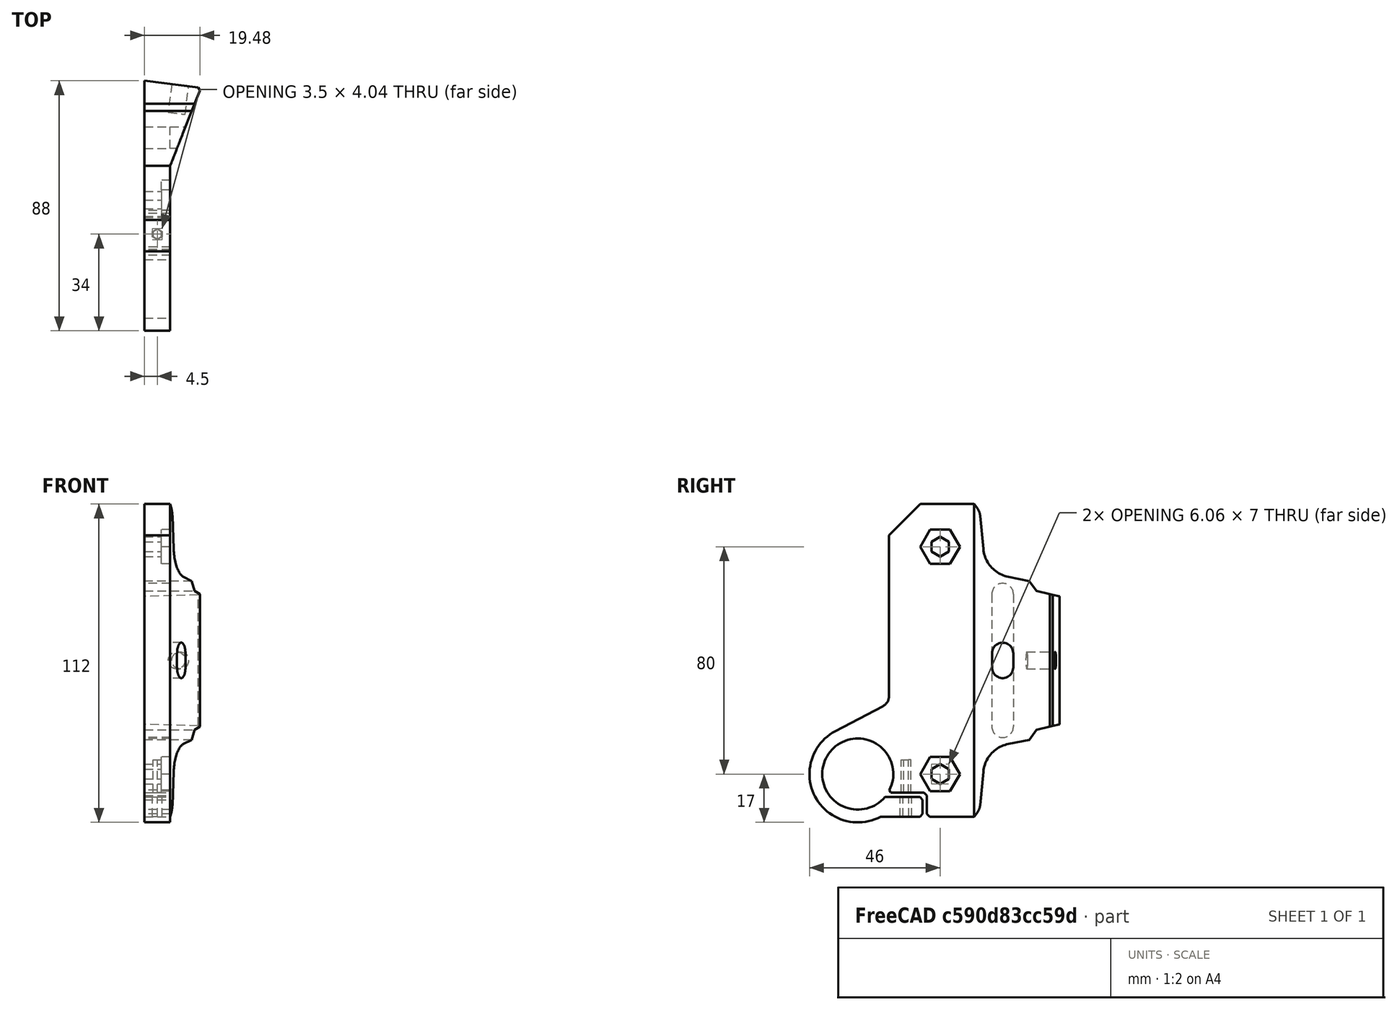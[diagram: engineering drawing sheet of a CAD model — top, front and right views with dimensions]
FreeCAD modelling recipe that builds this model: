
FCSTD DOCUMENT  (FreeCAD 0.19R)
Label: TailLightBracketForRack_80mmDual
License: All rights reserved
LicenseURL: http://en.wikipedia.org/wiki/All_rights_reserved
objects: Sketcher::SketchObject×12, PartDesign::Pocket×11, PartDesign::Fillet×3, PartDesign::Chamfer×3, PartDesign::Pad×1, PartDesign::Body×1, App::Part×1, Mesh::Feature×1
note: 49 computed .brp shape members not serialized (recipe doc carries the construction recipe); baked Part::Feature solids carry a one-line shape summary decoded from their .brp

FEATURE [Sketcher::SketchObject] Sketch007  label="body"
  FullyConstrained = true
  MapMode = 5
  Support = -> [XY_Plane001]
  sketch-geometry (5):
    g0: LineSegment StartX=9 StartY=0 StartZ=0 EndX=19.8509 EndY=27.5626 EndZ=0
    g1: LineSegment StartX=19.8509 StartY=27.5626 StartZ=0 EndX=0 EndY=30 EndZ=0
    g2: LineSegment StartX=9 StartY=0 StartZ=0 EndX=9 EndY=-60 EndZ=0
    g3: LineSegment StartX=9 StartY=-60 StartZ=0 EndX=0 EndY=-60 EndZ=0
    g4: LineSegment StartX=0 StartY=-60 StartZ=0 EndX=0 EndY=30 EndZ=0
  constraints (15):
    c: PointOnObject(g0,g-1)
    c: Angle(g1) = 3.01942
    c: Coincident(g0,g1)
    c: DistanceY(g1) = 30
    c: Distance(g1) = 20
    c: Coincident(g2,g0)
    c: Vertical(g2)
    c: Coincident(g3,g2)
    c: PointOnObject(g3,g-2)
    c: Horizontal(g3)
    c: Coincident(g4,g3)
    c: Vertical(g4)
    c: Coincident(g4,g1)
    c: Distance(g3) = 9
    c: DistanceY(g3) = -60
FEATURE [PartDesign::Pad] Pad
  AllowMultiFace = false
  Direction = (1,1,1)
  Length = 200
  Length2 = 100
  Midplane = true
  Profile = -> Sketch007
  Type = 0
FEATURE [Sketcher::SketchObject] Sketch012  label="bodypocket1"
  FullyConstrained = false
  MapMode = 5
  Placement = pos=(-30,0,0) rot=(0.57735,-0.57735,-0.57735;2.0944rad)
  sketch-geometry (23):
    g0: LineSegment StartX=-105.867 StartY=145.328 StartZ=0 EndX=-105.867 EndY=-150.387 EndZ=0
    g1: LineSegment StartX=-30.0416 StartY=-22.5 StartZ=0 EndX=-30.0416 EndY=22.5 EndZ=0
    g2: LineSegment StartX=195.435 StartY=55 StartZ=0 EndX=195.435 EndY=105.454 EndZ=0
    g3: LineSegment StartX=195.435 StartY=105.454 StartZ=0 EndX=-105.867 EndY=145.328 EndZ=0
    g4: LineSegment StartX=195.435 StartY=55 StartZ=0 EndX=0 EndY=55 EndZ=0
    g5: LineSegment StartX=0 StartY=55 StartZ=0 EndX=-21.9085 EndY=24.4142 EndZ=0
    g6: LineSegment StartX=33 StartY=-55 StartZ=0 EndX=0 EndY=-55 EndZ=0
    g7: LineSegment StartX=0 StartY=-55 StartZ=0 EndX=-21.9085 EndY=-24.4142 EndZ=0
    g8: ArcOfCircle CenterX=41 CenterY=-40 CenterZ=0 NormalX=0 NormalY=0 NormalZ=1 AngleXU=0 Radius=17 StartAngle=4.22243 EndAngle=7.36952
    g9: LineSegment StartX=48.9175 StartY=-24.9563 StartZ=0 EndX=30 EndY=-15 EndZ=0
    g10: Circle CenterX=41 CenterY=-40 CenterZ=0 NormalX=0 NormalY=0 NormalZ=1 AngleXU=0 Radius=12.5
    g11: LineSegment StartX=150.469 StartY=0 StartZ=0 EndX=97.2937 EndY=-143.387 EndZ=0
    g12: LineSegment StartX=97.2937 StartY=-143.387 StartZ=0 EndX=-105.867 EndY=-150.387 EndZ=0
    g13: LineSegment StartX=30 StartY=0 StartZ=0 EndX=150.469 EndY=0 EndZ=0
    g14: LineSegment StartX=-21.9085 StartY=24.4142 StartZ=0 EndX=-30.0416 EndY=22.5 EndZ=0
    g15: LineSegment StartX=-21.9085 StartY=-24.4142 StartZ=0 EndX=-30.0416 EndY=-22.5 EndZ=0
    g16: ArcOfCircle CenterX=-9 CenterY=23.25 CenterZ=0 NormalX=0 NormalY=0 NormalZ=1 AngleXU=0 Radius=3.75 StartAngle=0 EndAngle=3.14159
    g17: ArcOfCircle CenterX=-9 CenterY=-23.25 CenterZ=0 NormalX=0 NormalY=0 NormalZ=1 AngleXU=0 Radius=3.75 StartAngle=3.14159 EndAngle=6.28319
    g18: LineSegment StartX=-12.75 StartY=23.25 StartZ=0 EndX=-12.75 EndY=-23.25 EndZ=0
    g19: LineSegment StartX=-5.25 StartY=23.25 StartZ=0 EndX=-5.25 EndY=-23.25 EndZ=0
    g20: LineSegment StartX=-14.9249 StartY=27 StartZ=0 EndX=-4.09953 EndY=27 EndZ=0
    g21: LineSegment StartX=-14.2475 StartY=-27 StartZ=0 EndX=-3.85948 EndY=-27 EndZ=0
    g22: LineSegment StartX=30 StartY=-15 StartZ=0 EndX=30 EndY=0 EndZ=0
  constraints (50):
    c: Symmetric(g1,g1,g-1)
    c: Distance(g1) = 45
    c: Vertical(g0)
    c: Vertical(g2)
    c: Coincident(g3,g2)
    c: Coincident(g3,g0)
    c: PointOnObject(g4,g-2)
    c: Coincident(g4,g5)
    c: PointOnObject(g6,g-2)
    c: Coincident(g7,g6)
    c: DistanceX(g9) = 30
    c: Tangent(g9,g8) = -1.5708
    c: Diameter(g8) = 34
    c: Coincident(g10,g8)
    c: Diameter(g10) = 25
    c: DistanceY(g9) = -15
    c: Coincident(g11,g12)
    c: Coincident(g12,g0)
    c: PointOnObject(g13,g-1)
    c: Coincident(g11,g13)
    c: Symmetric(g5,g7,g-1)
    c: Coincident(g14,g5)
    c: Coincident(g14,g1)
    c: Coincident(g15,g7)
    c: Coincident(g15,g1)
    c: Tangent(g16,g19) = 1.5708
    c: Tangent(g16,g18) = -1.5708
    c: Tangent(g18,g17) = -1.5708
    c: Tangent(g19,g17) = 1.5708
    c: Vertical(g18)
    c: Distance(g17,g18) = 7.5
    c: Symmetric(g16,g17,g-1)
    c: DistanceX(g16) = -9
    c: Horizontal(g20)
    c: Tangent(g16,g20)
    c: Horizontal(g21)
    c: Tangent(g21,g17)
    c: DistanceY(g6) = -55
    c: DistanceY(g4) = 55
    c: Horizontal(g4)
    c: Horizontal(g6)
    c: Coincident(g4,g2)
    c: Coincident(g8,g6)
    c: DistanceY(g8) = -40
    c: Distance(g21,g20) = 54
    c: DistanceX(g8) = 41
    c: Horizontal(g13)
    c: Coincident(g22,g9)
    c: Coincident(g22,g13)
    c: Vertical(g22)
FEATURE [Sketcher::SketchObject] Sketch013  label="MountHole"
  FullyConstrained = true
  MapMode = 5
  Placement = pos=(3.62883,29.5544,0) rot=(0.043208,0.706446,0.706446;3.05523rad)
  sketch-geometry (1):
    g0: Circle CenterX=-9 CenterY=0 CenterZ=0 NormalX=0 NormalY=0 NormalZ=1 AngleXU=0 Radius=3
  constraints (3):
    c: PointOnObject(g0,g-1)
    c: Diameter(g0) = 6
    c: DistanceX(g0) = -9
FEATURE [PartDesign::Pocket] Pocket
  BaseFeature = -> Pad
  Length = 10
  Length2 = 100
  Profile = -> Sketch012
  Type = 1
FEATURE [Sketcher::SketchObject] Sketch019  label="bodypocket2"
  FullyConstrained = false
  MapMode = 5
  Placement = pos=(9,0,0) rot=(0.57735,0.57735,0.57735;2.0944rad)
  Support = -> [Pocket]
  sketch-geometry (4):
    g0: LineSegment StartX=-72.8805 StartY=81.5644 StartZ=0 EndX=-30 EndY=81.5644 EndZ=0
    g1: LineSegment StartX=-30 StartY=81.5644 StartZ=0 EndX=-30 EndY=0 EndZ=0
    g2: LineSegment StartX=-30 StartY=0 StartZ=0 EndX=-72.8805 EndY=0 EndZ=0
    g3: LineSegment StartX=-72.8805 StartY=0 StartZ=0 EndX=-72.8805 EndY=81.5644 EndZ=0
  constraints (10):
    c: Coincident(g0,g1)
    c: Coincident(g1,g2)
    c: Coincident(g2,g3)
    c: Coincident(g3,g0)
    c: Horizontal(g0)
    c: Horizontal(g2)
    c: Vertical(g1)
    c: Vertical(g3)
    c: PointOnObject(g1,g-1)
    c: DistanceX(g1) = -30
FEATURE [PartDesign::Pocket] Pocket001
  BaseFeature = -> Pocket
  Length = 5
  Length2 = 100
  Profile = -> Sketch019
  Type = 1
FEATURE [Sketcher::SketchObject] Sketch015  label="lightholes"
  FullyConstrained = true
  MapMode = 5
  Placement = pos=(0,0,0) rot=(0.57735,-0.57735,-0.57735;2.0944rad)
  Support = -> [Pocket001]
  sketch-geometry (14):
    g0: LineSegment StartX=12 StartY=36.5 StartZ=0 EndX=15.0311 EndY=38.25 EndZ=0
    g1: LineSegment StartX=15.0311 StartY=38.25 StartZ=0 EndX=15.0311 EndY=41.75 EndZ=0
    g2: LineSegment StartX=15.0311 StartY=41.75 StartZ=0 EndX=12 EndY=43.5 EndZ=0
    g3: LineSegment StartX=12 StartY=43.5 StartZ=0 EndX=8.96891 EndY=41.75 EndZ=0
    g4: LineSegment StartX=8.96891 StartY=41.75 StartZ=0 EndX=8.96891 EndY=38.25 EndZ=0
    g5: LineSegment StartX=8.96891 StartY=38.25 StartZ=0 EndX=12 EndY=36.5 EndZ=0
    g6: Circle CenterX=12 CenterY=40 CenterZ=0 NormalX=0 NormalY=0 NormalZ=1 AngleXU=0 Radius=3.5
    g7: LineSegment StartX=12 StartY=-43.5 StartZ=0 EndX=15.0311 EndY=-41.75 EndZ=0
    g8: LineSegment StartX=15.0311 StartY=-41.75 StartZ=0 EndX=15.0311 EndY=-38.25 EndZ=0
    g9: LineSegment StartX=15.0311 StartY=-38.25 StartZ=0 EndX=12 EndY=-36.5 EndZ=0
    g10: LineSegment StartX=12 StartY=-36.5 StartZ=0 EndX=8.96891 EndY=-38.25 EndZ=0
    g11: LineSegment StartX=8.96891 StartY=-38.25 StartZ=0 EndX=8.96891 EndY=-41.75 EndZ=0
    g12: LineSegment StartX=8.96891 StartY=-41.75 StartZ=0 EndX=12 EndY=-43.5 EndZ=0
    g13: Circle CenterX=12 CenterY=-40 CenterZ=0 NormalX=0 NormalY=0 NormalZ=1 AngleXU=0 Radius=3.5
  constraints (33):
    c: Coincident(g0,g1)
    c: Coincident(g1,g2)
    c: Coincident(g2,g3)
    c: Coincident(g3,g4)
    c: Coincident(g4,g5)
    c: Coincident(g5,g0)
    c: Equal(g0, g1-g5) x5
    c: PointOnObject(g0,g6)
    c: PointOnObject(g1,g6)
    c: PointOnObject(g2,g6)
    c: PointOnObject(g3,g6)
    c: PointOnObject(g4,g6)
    c: PointOnObject(g5,g6)
    c: Coincident(g7,g8)
    c: Coincident(g8,g9)
    c: Coincident(g9,g10)
    c: Coincident(g10,g11)
    c: Coincident(g11,g12)
    c: Coincident(g12,g7)
    c: Equal(g7, g8-g12) x5
    c: PointOnObject(g7,g13)
    c: PointOnObject(g8,g13)
    c: PointOnObject(g9,g13)
    c: PointOnObject(g10,g13)
    c: PointOnObject(g11,g13)
    c: PointOnObject(g12,g13)
    c: Vertical(g8)
    c: Vertical(g1)
    c: Diameter(g6) = 7
    c: Equal(g6,g13)
    c: Symmetric(g6,g13,g-1)
    c: Distance(g6,g13) = 80
    c: DistanceX(g6) = 12
FEATURE [PartDesign::Pocket] Pocket002
  BaseFeature = -> Pocket001
  Length = 5
  Length2 = 100
  Profile = -> Sketch015
  Type = 1
FEATURE [Sketcher::SketchObject] Sketch021  label="lightSlot"
  FullyConstrained = false
  MapMode = 5
  Placement = pos=(0,0,0) rot=(0.57735,-0.57735,-0.57735;2.0944rad)
  Support = -> [Pocket002]
  sketch-geometry (6):
    g0: ArcOfCircle CenterX=-10 CenterY=23.325 CenterZ=0 NormalX=0 NormalY=0 NormalZ=1 AngleXU=0 Radius=3.8 StartAngle=-2.836e-12 EndAngle=3.14159
    g1: ArcOfCircle CenterX=-10 CenterY=-23.325 CenterZ=0 NormalX=0 NormalY=0 NormalZ=1 AngleXU=0 Radius=3.8 StartAngle=3.14159 EndAngle=6.28319
    g2: LineSegment StartX=-13.8 StartY=23.325 StartZ=0 EndX=-13.8 EndY=-23.325 EndZ=0
    g3: LineSegment StartX=-6.2 StartY=23.325 StartZ=0 EndX=-6.2 EndY=-23.325 EndZ=0
    g4: LineSegment StartX=-21.665 StartY=27.125 StartZ=0 EndX=-13.4286 EndY=27.125 EndZ=0
    g5: LineSegment StartX=-21.9335 StartY=-27.125 StartZ=0 EndX=-10 EndY=-27.125 EndZ=0
  constraints (14):
    c: Tangent(g0,g3) = 1.5708
    c: Tangent(g0,g2) = -1.5708
    c: Tangent(g2,g1) = -1.5708
    c: Tangent(g3,g1) = 1.5708
    c: Vertical(g2)
    c: Distance(g0,g0) = 7.6
    c: Symmetric(g0,g1,g-1)
    c: Horizontal(g4)
    c: Tangent(g4,g0)
    c: PointOnObject(g5,g1)
    c: Horizontal(g5)
    c: Tangent(g5,g1)
    c: Distance(g5,g4) = 54.25
    c: DistanceX(g0) = -10
FEATURE [PartDesign::Pocket] Pocket003
  BaseFeature = -> Pocket002
  Length = 9
  Length2 = 100
  Profile = -> Sketch021
  Type = 0
FEATURE [PartDesign::Pocket] Pocket004
  BaseFeature = -> Pocket003
  Length = 10
  Length2 = 100
  Profile = -> Sketch013
  Type = 0
FEATURE [Sketcher::SketchObject] Sketch  label="pinchslot"
  FullyConstrained = false
  MapMode = 5
  Placement = pos=(0,0,0) rot=(0.57735,-0.57735,-0.57735;2.0944rad)
  Support = -> [Pocket004]
  sketch-geometry (6):
    g0: LineSegment StartX=18.158 StartY=-56.8978 StartZ=0 EndX=18.158 EndY=-48.0563 EndZ=0
    g1: LineSegment StartX=18.158 StartY=-48.0563 StartZ=0 EndX=46.2212 EndY=-48.0563 EndZ=0
    g2: LineSegment StartX=46.2212 StartY=-48.0563 StartZ=0 EndX=46.9623 EndY=-46.5563 EndZ=0
    g3: LineSegment StartX=46.9623 StartY=-46.5563 StartZ=0 EndX=16.658 EndY=-46.5563 EndZ=0
    g4: LineSegment StartX=16.658 StartY=-46.5563 StartZ=0 EndX=16.658 EndY=-57.2519 EndZ=0
    g5: LineSegment StartX=16.658 StartY=-57.2519 StartZ=0 EndX=18.158 EndY=-56.8978 EndZ=0
  constraints (12):
    c: Coincident(g0,g1)
    c: Coincident(g1,g2)
    c: Coincident(g2,g3)
    c: Coincident(g3,g4)
    c: Coincident(g4,g5)
    c: Coincident(g5,g0)
    c: Parallel(g4,g0)
    c: Parallel(g1,g3)
    c: Distance(g0,g3) = 1.5
    c: Distance(g0,g4) = 1.5
    c: Perpendicular(g0,g1)
    c: Vertical(g4)
FEATURE [PartDesign::Pocket] Pocket005
  BaseFeature = -> Pocket004
  Length = 5
  Length2 = 100
  Profile = -> Sketch
  Type = 1
FEATURE [Sketcher::SketchObject] Sketch017
  FullyConstrained = true
  MapMode = 5
  Placement = pos=(0,0,-55) rot=(1,0,0;3.14159rad)
  Support = -> [Pocket005]
  sketch-geometry (7):
    g0: LineSegment StartX=6.25 StartY=22.9896 StartZ=0 EndX=6.25 EndY=25.0104 EndZ=0
    g1: LineSegment StartX=6.25 StartY=25.0104 StartZ=0 EndX=4.5 EndY=26.0207 EndZ=0
    g2: LineSegment StartX=4.5 StartY=26.0207 StartZ=0 EndX=2.75 EndY=25.0104 EndZ=0
    g3: LineSegment StartX=2.75 StartY=25.0104 StartZ=0 EndX=2.75 EndY=22.9896 EndZ=0
    g4: LineSegment StartX=2.75 StartY=22.9896 StartZ=0 EndX=4.5 EndY=21.9793 EndZ=0
    g5: LineSegment StartX=4.5 StartY=21.9793 StartZ=0 EndX=6.25 EndY=22.9896 EndZ=0
    g6: Circle CenterX=4.5 CenterY=24 CenterZ=0 NormalX=0 NormalY=0 NormalZ=1 AngleXU=0 Radius=2.02073
  constraints (17):
    c: Coincident(g0,g1)
    c: Coincident(g1,g2)
    c: Coincident(g2,g3)
    c: Coincident(g3,g4)
    c: Coincident(g4,g5)
    c: Coincident(g5,g0)
    c: Equal(g0, g1-g5) x5
    c: PointOnObject(g0,g6)
    c: PointOnObject(g1,g6)
    c: PointOnObject(g2,g6)
    c: PointOnObject(g3,g6)
    c: PointOnObject(g4,g6)
    c: PointOnObject(g5,g6)
    c: Distance(g1,g3) = 3.5
    c: DistanceX(g6) = 4.5
    c: Vertical(g3)
    c: DistanceY(g6) = 24
FEATURE [Sketcher::SketchObject] Sketch018
  FullyConstrained = true
  MapMode = 5
  Placement = pos=(0,0,-55) rot=(1,0,0;3.14159rad)
  Support = -> [Pocket005]
  sketch-geometry (7):
    g0: LineSegment StartX=4.5 StartY=22.3257 StartZ=0 EndX=5.95 EndY=23.1628 EndZ=0
    g1: LineSegment StartX=5.95 StartY=23.1628 StartZ=0 EndX=5.95 EndY=24.8372 EndZ=0
    g2: LineSegment StartX=5.95 StartY=24.8372 StartZ=0 EndX=4.5 EndY=25.6743 EndZ=0
    g3: LineSegment StartX=4.5 StartY=25.6743 StartZ=0 EndX=3.05 EndY=24.8372 EndZ=0
    g4: LineSegment StartX=3.05 StartY=24.8372 StartZ=0 EndX=3.05 EndY=23.1628 EndZ=0
    g5: LineSegment StartX=3.05 StartY=23.1628 StartZ=0 EndX=4.5 EndY=22.3257 EndZ=0
    g6: Circle CenterX=4.5 CenterY=24 CenterZ=0 NormalX=0 NormalY=0 NormalZ=1 AngleXU=0 Radius=1.67432
  constraints (17):
    c: Coincident(g0,g1)
    c: Coincident(g1,g2)
    c: Coincident(g2,g3)
    c: Coincident(g3,g4)
    c: Coincident(g4,g5)
    c: Coincident(g5,g0)
    c: Equal(g0, g1-g5) x5
    c: PointOnObject(g0,g6)
    c: PointOnObject(g1,g6)
    c: PointOnObject(g2,g6)
    c: PointOnObject(g3,g6)
    c: PointOnObject(g4,g6)
    c: PointOnObject(g5,g6)
    c: Vertical(g1)
    c: Distance(g1,g3) = 2.9
    c: DistanceX(g6) = 4.5
    c: DistanceY(g6) = 24
FEATURE [Sketcher::SketchObject] Sketch022  label="wireslot"
  FullyConstrained = true
  MapMode = 5
  Placement = pos=(9,0,0) rot=(0.57735,-0.57735,-0.57735;2.0944rad)
  sketch-geometry (4):
    g0: ArcOfCircle CenterX=-10 CenterY=2.5 CenterZ=0 NormalX=0 NormalY=0 NormalZ=1 AngleXU=0 Radius=3.75 StartAngle=0 EndAngle=3.14159
    g1: ArcOfCircle CenterX=-10 CenterY=-2.5 CenterZ=0 NormalX=0 NormalY=0 NormalZ=1 AngleXU=0 Radius=3.75 StartAngle=3.14159 EndAngle=6.28319
    g2: LineSegment StartX=-13.75 StartY=2.5 StartZ=0 EndX=-13.75 EndY=-2.5 EndZ=0
    g3: LineSegment StartX=-6.25 StartY=2.5 StartZ=0 EndX=-6.25 EndY=-2.5 EndZ=0
  constraints (9):
    c: Tangent(g0,g3) = 1.5708
    c: Tangent(g0,g2) = -1.5708
    c: Tangent(g2,g1) = -1.5708
    c: Tangent(g3,g1) = 1.5708
    c: Vertical(g2)
    c: Distance(g0,g0) = 7.5
    c: DistanceX(g0) = -10
    c: Symmetric(g0,g1,g-1)
    c: Distance(g2) = 5
FEATURE [Sketcher::SketchObject] Sketch023  label="boltcountersink"
  FullyConstrained = true
  MapMode = 5
  Placement = pos=(9,0,0) rot=(0.57735,0.57735,0.57735;2.0944rad)
  sketch-geometry (14):
    g0: LineSegment StartX=-8.5 StartY=33.9378 StartZ=0 EndX=-5 EndY=40 EndZ=0
    g1: LineSegment StartX=-5 StartY=40 StartZ=0 EndX=-8.5 EndY=46.0622 EndZ=0
    g2: LineSegment StartX=-8.5 StartY=46.0622 StartZ=0 EndX=-15.5 EndY=46.0622 EndZ=0
    g3: LineSegment StartX=-15.5 StartY=46.0622 StartZ=0 EndX=-19 EndY=40 EndZ=0
    g4: LineSegment StartX=-19 StartY=40 StartZ=0 EndX=-15.5 EndY=33.9378 EndZ=0
    g5: LineSegment StartX=-15.5 StartY=33.9378 StartZ=0 EndX=-8.5 EndY=33.9378 EndZ=0
    g6: Circle CenterX=-12 CenterY=40 CenterZ=0 NormalX=0 NormalY=0 NormalZ=1 AngleXU=0 Radius=7
    g7: LineSegment StartX=-8.5 StartY=-46.0622 StartZ=0 EndX=-5 EndY=-40 EndZ=0
    g8: LineSegment StartX=-5 StartY=-40 StartZ=0 EndX=-8.5 EndY=-33.9378 EndZ=0
    g9: LineSegment StartX=-8.5 StartY=-33.9378 StartZ=0 EndX=-15.5 EndY=-33.9378 EndZ=0
    g10: LineSegment StartX=-15.5 StartY=-33.9378 StartZ=0 EndX=-19 EndY=-40 EndZ=0
    g11: LineSegment StartX=-19 StartY=-40 StartZ=0 EndX=-15.5 EndY=-46.0622 EndZ=0
    g12: LineSegment StartX=-15.5 StartY=-46.0622 StartZ=0 EndX=-8.5 EndY=-46.0622 EndZ=0
    g13: Circle CenterX=-12 CenterY=-40 CenterZ=0 NormalX=0 NormalY=0 NormalZ=1 AngleXU=0 Radius=7
  constraints (33):
    c: Coincident(g0,g1)
    c: Coincident(g1,g2)
    c: Coincident(g2,g3)
    c: Coincident(g3,g4)
    c: Coincident(g4,g5)
    c: Coincident(g5,g0)
    c: Equal(g0, g1-g5) x5
    c: PointOnObject(g0,g6)
    c: PointOnObject(g1,g6)
    c: PointOnObject(g2,g6)
    c: PointOnObject(g3,g6)
    c: PointOnObject(g4,g6)
    c: PointOnObject(g5,g6)
    c: Coincident(g7,g8)
    c: Coincident(g8,g9)
    c: Coincident(g9,g10)
    c: Coincident(g10,g11)
    c: Coincident(g11,g12)
    c: Coincident(g12,g7)
    c: Equal(g7, g8-g12) x5
    c: PointOnObject(g7,g13)
    c: PointOnObject(g8,g13)
    c: PointOnObject(g9,g13)
    c: PointOnObject(g10,g13)
    c: PointOnObject(g11,g13)
    c: PointOnObject(g12,g13)
    c: Symmetric(g6,g13,g-1)
    c: Distance(g6,g13) = 80
    c: DistanceX(g6) = -12
    c: Horizontal(g2)
    c: Horizontal(g9)
    c: Diameter(g13) = 14
    c: Equal(g13,g6)
FEATURE [Sketcher::SketchObject] Sketch025  label="rackclear"
  FullyConstrained = false
  MapMode = 5
  Placement = pos=(0,0,0) rot=(0.57735,-0.57735,-0.57735;2.0944rad)
  sketch-geometry (8):
    g0: LineSegment StartX=-43.6976 StartY=23.0953 StartZ=0 EndX=-4 EndY=31 EndZ=0
    g1: LineSegment StartX=0 StartY=72.5766 StartZ=0 EndX=-72.8875 EndY=27.9359 EndZ=0
    g2: LineSegment StartX=-72.8875 StartY=27.9359 StartZ=0 EndX=-85.9079 EndY=-106.21 EndZ=0
    g3: LineSegment StartX=-85.9079 StartY=-106.21 StartZ=0 EndX=0 EndY=-72.5766 EndZ=0
    g4: LineSegment StartX=0 StartY=-72.5766 StartZ=0 EndX=-4 EndY=-31 EndZ=0
    g5: LineSegment StartX=-4 StartY=-31 StartZ=0 EndX=-43.6976 EndY=-23.0953 EndZ=0
    g6: LineSegment StartX=-43.6976 StartY=-23.0953 StartZ=0 EndX=-43.6976 EndY=23.0953 EndZ=0
    g7: LineSegment StartX=-4 StartY=31 StartZ=0 EndX=0 EndY=72.5766 EndZ=0
  constraints (14):
    c: PointOnObject(g1,g-2)
    c: Coincident(g1,g2)
    c: Coincident(g2,g3)
    c: Coincident(g3,g4)
    c: Coincident(g4,g5)
    c: Coincident(g5,g6)
    c: Coincident(g6,g0)
    c: Symmetric(g0,g5,g-1)
    c: Symmetric(g0,g4,g-1)
    c: Coincident(g7,g0)
    c: Coincident(g7,g1)
    c: DistanceX(g4) = -4
    c: DistanceY(g0) = 31
    c: Symmetric(g3,g1,g-1)
FEATURE [PartDesign::Pocket] Pocket006
  BaseFeature = -> Pocket005
  Length = 20
  Length2 = 100
  Profile = -> Sketch018
  Type = 0
FEATURE [PartDesign::Pocket] Pocket007
  BaseFeature = -> Pocket006
  Length = 8
  Length2 = 100
  Profile = -> Sketch017
  Type = 0
FEATURE [PartDesign::Pocket] Pocket008
  BaseFeature = -> Pocket007
  Length = 5
  Length2 = 100
  Profile = -> Sketch022
  Type = 1
FEATURE [PartDesign::Pocket] Pocket009
  BaseFeature = -> Pocket008
  Length = 3
  Length2 = 100
  Profile = -> Sketch023
  Type = 0
FEATURE [PartDesign::Pocket] Pocket010
  BaseFeature = -> Pocket009
  Length = 5
  Length2 = 100
  Profile = -> Sketch025
  Type = 1
FEATURE [PartDesign::Fillet] Fillet
  Base = -> Pocket010 [Edge21,Edge36]
  BaseFeature = -> Pocket010
  Radius = 11
  SupportTransform = false
FEATURE [PartDesign::Fillet] Fillet001
  Base = -> Fillet [Edge21,Edge56]
  BaseFeature = -> Fillet
  Radius = 5
  SupportTransform = false
FEATURE [PartDesign::Fillet] Fillet002
  Base = -> Fillet001 [Edge127]
  BaseFeature = -> Fillet001
  Radius = 4
  SupportTransform = false
FEATURE [PartDesign::Chamfer] Chamfer
  Angle = 45
  Base = -> Fillet002 [Edge84,Edge74,Edge72,Edge70,Edge61]
  BaseFeature = -> Fillet002
  ChamferType = 0
  FlipDirection = false
  Size = 1
  Size2 = 1
  SupportTransform = false
FEATURE [PartDesign::Chamfer] Chamfer001
  Angle = 45
  Base = -> Chamfer [Edge67]
  BaseFeature = -> Chamfer
  ChamferType = 0
  FlipDirection = false
  Size = 11
  Size2 = 1
  SupportTransform = false
FEATURE [PartDesign::Chamfer] Chamfer002
  Angle = 45
  Base = -> Chamfer001 [Edge54]
  BaseFeature = -> Chamfer001
  ChamferType = 0
  FlipDirection = false
  Size = 1
  Size2 = 1
  SupportTransform = false
FEATURE [PartDesign::Body] PadBody
  Group = -> [Sketch007,Pad,Sketch012,Sketch013,Pocket,Sketch,Sketch015,Sketch017,Sketch018,Sketch019,Pocket001,Pocket002,Sketch021,Pocket003,Pocket004,Pocket005,Sketch022,Sketch023,Sketch025,Pocket006,Pocket007,Pocket008,Pocket009,Pocket010,Fillet,Fillet001,Fillet002,Chamfer,Chamfer001,Chamfer002]
  Origin = -> Origin001
  Tip = -> Chamfer002
FEATURE [App::Part] Part
  Group = -> [PadBody]
  Origin = -> Origin
FEATURE [Mesh::Feature] Mesh  label="Chamfer002 (Meshed)"
